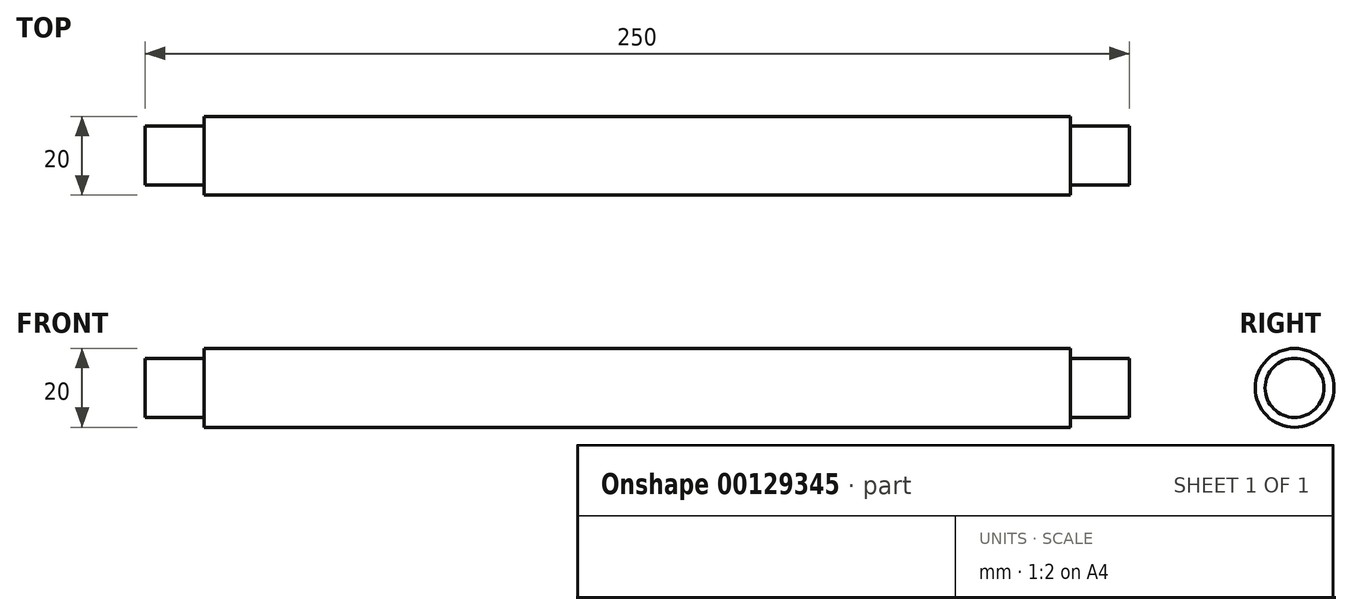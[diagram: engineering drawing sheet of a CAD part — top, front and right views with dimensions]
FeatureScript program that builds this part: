
annotation { "Feature Type Name" : "Feature", "Feature Type Description" : "" }
export const myFeature = defineFeature(function(context is Context, id is Id, definition is map)
    precondition{}
    {
        {
            var Q0;
            Q0=qCreatedBy(makeId("Right.planeOp"),FACE);
            var sketch = newSketch(context, id + "F0", { "sketchPlane" : qUnion([Q0])});
            skCircle(sketch, "E0", {"center": v(0, 0) * mm, "radius": 10 * mm});
            skCircle(sketch, "E1", {"center": v(0, 0) * mm, "radius": 7.5 * mm});
            skSolve(sketch);
        }
        {
            var Q0;
            Q0=makeQuery(id+"F0.imprint","IMPRINT",FACE,{"disambiguationData":[TD([[makeQuery(id+"F0.imprint","IMPRINT",EDGE,{"derivedFrom":sQuery(id+"F0.wireOp",EDGE,"E1")}),1.0]])]});
            extrude(context, id + "F1", {"entities" : qUnion([Q0]), "depth" : 15 * mm, "hasSecondDirection" : true, "secondDirectionOppositeDirection" : true, "secondDirectionDepth" : 235 * mm});
        }
        {
            var Q0;
            Q0=makeQuery(id+"F0.imprint","IMPRINT",FACE,{"disambiguationData":[TD([[makeQuery(id+"F0.imprint","IMPRINT",EDGE,{"derivedFrom":sQuery(id+"F0.wireOp",EDGE,"E0")}),1.0]])]});
            extrude(context, id + "F2", {"entities" : qUnion([Q0]), "operationType" : NewBodyOperationType.ADD, "oppositeDirection" : true, "depth" : 220 * mm});
        }
    });
